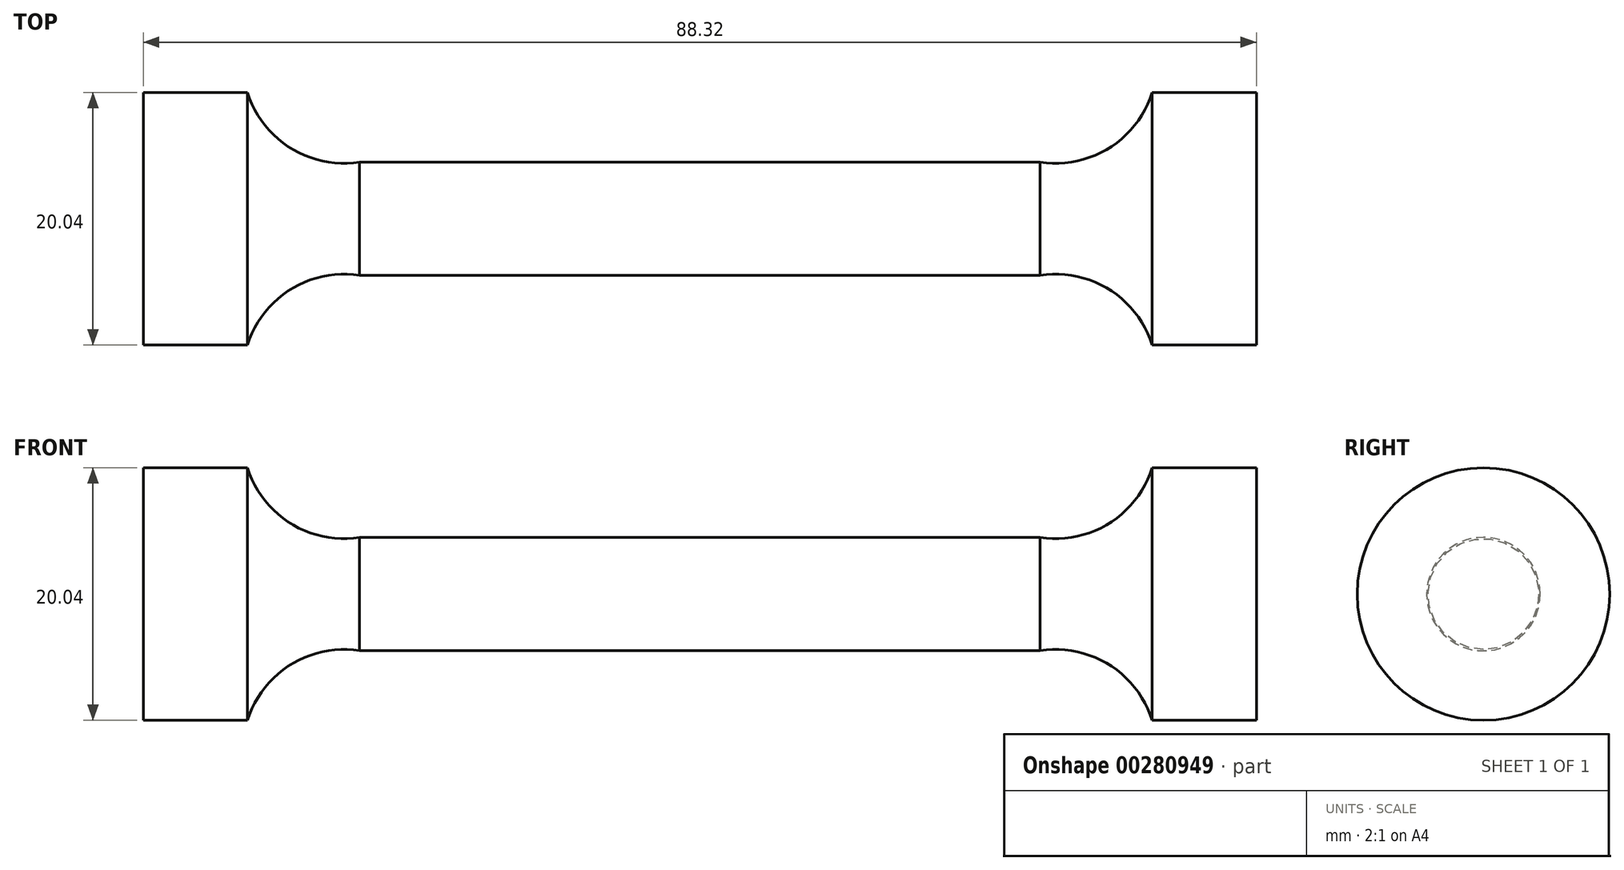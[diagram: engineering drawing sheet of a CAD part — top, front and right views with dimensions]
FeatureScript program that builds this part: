
annotation { "Feature Type Name" : "Feature", "Feature Type Description" : "" }
export const myFeature = defineFeature(function(context is Context, id is Id, definition is map)
    precondition{}
    {
        {
            var Q0;
            Q0=qCreatedBy(makeId("Front.planeOp"),FACE);
            var sketch = newSketch(context, id + "F0", { "sketchPlane" : qUnion([Q0])});
            skLineSegment(sketch, "E0", {"start": v(0, 0) * mm, "end": v(44.16, 0) * mm});
            skLineSegment(sketch, "E1", {"start": v(44.16, 0) * mm, "end": v(44.16, 10.02) * mm});
            skLineSegment(sketch, "E2", {"start": v(44.16, 10.02) * mm, "end": v(35.89, 10.02) * mm});
            skArc(sketch, "E3", {"start": v(27, 4.5) * mm, "mid": v(32.47, 5.6) * mm, "end": v(35.89, 10.02) * mm});
            skLineSegment(sketch, "E4", {"start": v(27, 4.5) * mm, "end": v(0, 4.5) * mm});
            skLineSegment(sketch, "E5.MirrorCS", {"start": v(0, 0) * mm, "end": v(-44.16, 0) * mm});
            skLineSegment(sketch, "E6.MirrorCS", {"start": v(-27, 4.5) * mm, "end": v(0, 4.5) * mm});
            skLineSegment(sketch, "E7.MirrorCS", {"start": v(-44.16, 0) * mm, "end": v(-44.16, 10.02) * mm});
            skLineSegment(sketch, "E8.MirrorCS", {"start": v(-44.16, 10.02) * mm, "end": v(-35.89, 10.02) * mm});
            skArc(sketch, "E9.MirrorCS", {"start": v(-27, 4.5) * mm, "mid": v(-32.47, 5.6) * mm, "end": v(-35.89, 10.02) * mm});
            skSolve(sketch);
        }
        {
            var Q0;
            Q0=makeQuery(id+"F0.imprint","IMPRINT",FACE,{"disambiguationData":[TD([[makeQuery(id+"F0.imprint","IMPRINT",EDGE,{"derivedFrom":sQuery(id+"F0.wireOp",EDGE,"E0")}),1.0]])]});
            var Q1;
            Q1=sQuery(id+"F0.wireOp",EDGE,"E5.MirrorCS");
            revolve(context, id + "F1", {"entities" : qUnion([Q0]), "axis" : qUnion([Q1]), "revolveType" : RevolveType.FULL});
        }
    });
